# Revit family: 510160P-V2
name_source: partatom
category: Plumbing Fixtures
revit_build: Autodesk Revit 2015 (Build: 20140606_1530(x64)
units: mm (PartAtom-declared; Revit-internal decimal feet)

## types (1)
- Type 1
    Category = Grab bar
    DLB090011 = Stainless Steel
    Description = French manufacturer Delabie is a leader in the European sanitary ware market for non-domestic places. Water controls, solutions for disabled people, sanitary ware, for schools, leisure centres, offices, hospitals, airports…
    Features = Drop-down grab bar Ø 32mm. In the lowered position use as a grab bar, for standing up and assisting movement. For WCs or showers. Allows side access in the raised position. Dimensions : 650 x 230 x 105mm. Tube thickness: 1.5mm. Slowed down descent. Retained in upright position. Bacteriostatic 304 stainless steel tube. Stainless steel with UltraPolish bright polished finish, non-porous uniform surface for easy maintenance and hygiene. Fixings concealed by a 304 stainless steel cover plate, 4mm thick. Supplied with stainless steel screws for concrete walls. Tested to over 200kg. Maximum recommended user weight 135kg. 10 year warranty. CE marked.
    Finish = Bright polished
    Grade = CE
    IntegralAccessoryOptions = Backrest, toilet roll holder
    Manufacturer = DELABIE
    ManufacturerName = DELABIE
    Material = Stainless steel
    Model = Drop-down bar without leg L. 650mm
    Model number = 510160P
    Name = 510160P
    NominalHeight = 230 mm  [stored 0.754593 ft]
    NominalLength = 650 mm  [stored 2.13255 ft]
    NominalWidth = 105 mm  [stored 0.344488 ft]
    Polantis code = DLB090011
    ProductInformation = http://www.delabie.com
    SerialNumber = 3456330154550
    URL = http://www.delabie.com
    WarrantyDescription = Any manufacturing defect
    WarrantyDurationUnit = 10 years

note: [stored X ft] marks values corroborated as IEEE doubles in the binary element streams (Revit-internal decimal feet)

## geometry (parser evidence)
native form markers: Sweep x3
no freeform markers — native parametric forms only
